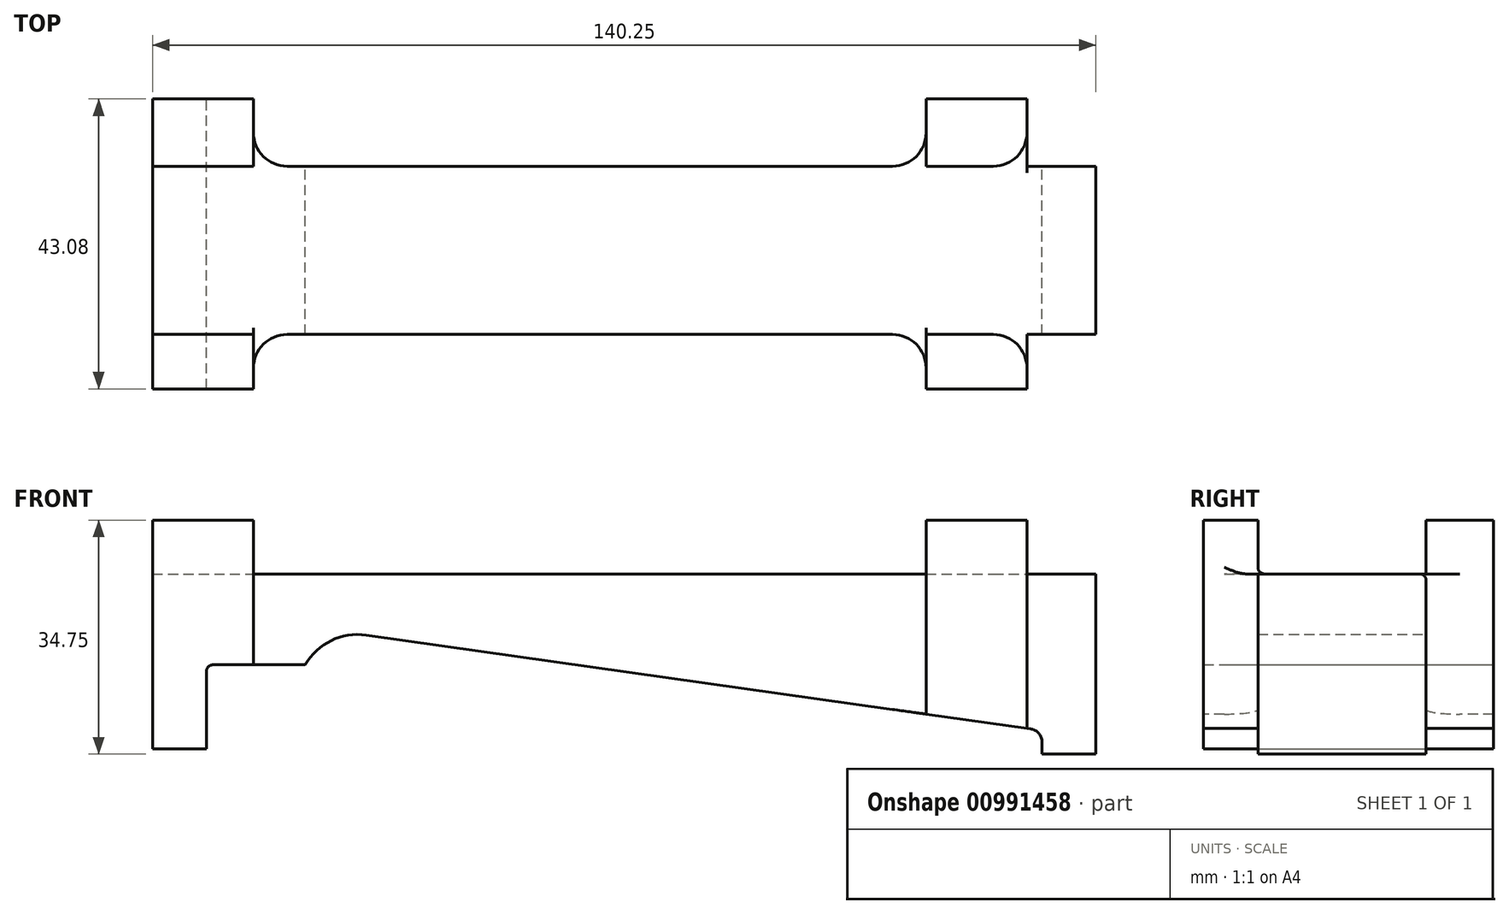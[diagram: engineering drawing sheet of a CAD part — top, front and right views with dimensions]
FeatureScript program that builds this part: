
annotation { "Feature Type Name" : "Feature", "Feature Type Description" : "" }
export const myFeature = defineFeature(function(context is Context, id is Id, definition is map)
    precondition{}
    {
        {
            var Q0;
            Q0=qCreatedBy(makeId("Front.planeOp"),FACE);
            var sketch = newSketch(context, id + "F0", { "sketchPlane" : qUnion([Q0])});
            skLineSegment(sketch, "E0", {"start": v(-65.44, 0) * mm, "end": v(89.84, 0) * mm, "construction": true});
            skArc(sketch, "E1", {"start": v(-48.74, 17.91) * mm, "mid": v(-53.94, 17.1) * mm, "end": v(-57.8, 13.5) * mm});
            skArc(sketch, "E2", {"start": v(51.75, 2) * mm, "mid": v(51.26, 3.31) * mm, "end": v(50.03, 3.98) * mm});
            skLineSegment(sketch, "E3", {"start": v(-48.74, 17.91) * mm, "end": v(50.03, 3.98) * mm});
            skLineSegment(sketch, "E4", {"start": v(-50, 9) * mm, "end": v(-61.37, 9) * mm, "construction": true});
            skPoint(sketch, "E5", {"position": v(-59, 9) * mm});
            skLineSegment(sketch, "E6", {"start": v(-59, 9) * mm, "end": v(-59, 24) * mm, "construction": true});
            skLineSegment(sketch, "E7", {"start": v(-72, 24) * mm, "end": v(-72, 0) * mm, "construction": true});
            skLineSegment(sketch, "E8", {"start": v(-72, 24) * mm, "end": v(-59, 24) * mm, "construction": true});
            skLineSegment(sketch, "E9", {"start": v(-81.75, 40) * mm, "end": v(68.2, 40) * mm, "construction": true});
            skLineSegment(sketch, "E10", {"start": v(-72, 13) * mm, "end": v(-59, 13) * mm, "construction": true});
            skLineSegment(sketch, "E11", {"start": v(-80.5, 27) * mm, "end": v(59.75, 27) * mm});
            skLineSegment(sketch, "E12", {"start": v(59.75, 27) * mm, "end": v(59.75, 0.25) * mm});
            skLineSegment(sketch, "E13", {"start": v(49.75, 2) * mm, "end": v(53.34, 2) * mm, "construction": true});
            skPoint(sketch, "E14", {"position": v(51.75, 2) * mm});
            skLineSegment(sketch, "E15", {"start": v(51.75, 2) * mm, "end": v(51.75, 0.25) * mm});
            skLineSegment(sketch, "E16", {"start": v(51.75, 0.25) * mm, "end": v(59.75, 0.25) * mm});
            skLineSegment(sketch, "E17", {"start": v(-57.8, 13.5) * mm, "end": v(-72.5, 13.5) * mm});
            skLineSegment(sketch, "E18", {"start": v(-72.5, 13.5) * mm, "end": v(-72.5, 1) * mm});
            skLineSegment(sketch, "E19", {"start": v(-72.5, 1) * mm, "end": v(-80.5, 1) * mm});
            skLineSegment(sketch, "E20", {"start": v(-80.5, 1) * mm, "end": v(-80.5, 27) * mm});
            skSolve(sketch);
        }
        {
            var Q0;
            Q0 = qSketchRegion(id + "F0", true);
            extrude(context, id + "F1", {"entities" : qUnion([Q0]), "depth" : 25 * mm, "offsetDistance" : 25 * mm});
        }
        {
            var Q0;
            Q0=makeQuery(id+"F1.opExtrude","SWEPT_FACE",FACE,{"disambiguationData":[OSD([sQuery(id+"F0.wireOp",EDGE,"E20")])]});
            var sketch = newSketch(context, id + "F2", { "sketchPlane" : qUnion([Q0])});
            skLineSegment(sketch, "E21", {"start": v(0, 27) * mm, "end": v(0, 35) * mm});
            skLineSegment(sketch, "E22", {"start": v(0, 35) * mm, "end": v(-10, 35) * mm});
            skLineSegment(sketch, "E23", {"start": v(-10, 35) * mm, "end": v(-10, 1) * mm});
            skLineSegment(sketch, "E24", {"start": v(-10, 1) * mm, "end": v(0, 1) * mm});
            skSolve(sketch);
        }
        {
            var Q0;
            Q0=makeQuery(id+"F2.imprint","IMPRINT",FACE,{"disambiguationData":[TD([[makeQuery(id+"F2.imprint","IMPRINT",EDGE,{"derivedFrom":sQuery(id+"F2.wireOp",EDGE,"E21")}),1.0]])]});
            extrude(context, id + "F3", {"entities" : qUnion([Q0]), "operationType" : NewBodyOperationType.ADD, "oppositeDirection" : true, "depth" : 130 * mm, "offsetDistance" : 25 * mm});
        }
        {
            var Q0;
            {var subQ2=sQuery(id+"F0.wireOp",EDGE,"E20");var subQ5=sQuery(id+"F0.wireOp",EDGE,"E1");var subQ7=sQuery(id+"F2.wireOp",EDGE,"E21");Q0=makeQuery(id+"F3.boolean.opBoolean","SPLIT",FACE,{"disambiguationData":[TD([makeQuery(id+"F1.opExtrude","SWEPT_FACE",FACE,{"disambiguationData":[OSD([subQ5])]})])],"derivedFrom":makeQuery(id+"F3.opExtrude","SWEPT_FACE",FACE,{"disambiguationData":[OSD([subQ2,subQ7])]})});}
            extrude(context, id + "F4", {"entities" : qUnion([Q0]), "operationType" : NewBodyOperationType.REMOVE, "oppositeDirection" : true, "depth" : 25 * mm, "offsetDistance" : 25 * mm});
        }
        {
            var Q0;
            {var subQ0=sQuery(id+"F0.wireOp",EDGE,"E20");var subQ1=sQuery(id+"F2.wireOp",EDGE,"E21");Q0=makeQuery(id+"F3.boolean.opBoolean","SPLIT",EDGE,{"disambiguationData":[topologyDisambiguationEdgeConnected([makeQuery(id+"F1.opExtrude","CAP_FACE",FACE,{"disambiguationData":[OSD([sQuery(id+"F0.wireOp",EDGE,"E1"),sQuery(id+"F0.wireOp",EDGE,"E2"),sQuery(id+"F0.wireOp",EDGE,"E3"),sQuery(id+"F0.wireOp",EDGE,"E11"),sQuery(id+"F0.wireOp",EDGE,"E12"),sQuery(id+"F0.wireOp",EDGE,"E15"),sQuery(id+"F0.wireOp",EDGE,"E16"),sQuery(id+"F0.wireOp",EDGE,"E17"),sQuery(id+"F0.wireOp",EDGE,"E18"),sQuery(id+"F0.wireOp",EDGE,"E19"),subQ0])],"isStart":true}),makeQuery(id+"F3.opExtrude","CAP_FACE",FACE,{"disambiguationData":[OSD([subQ0,subQ1,sQuery(id+"F2.wireOp",EDGE,"E22"),sQuery(id+"F2.wireOp",EDGE,"E23"),sQuery(id+"F2.wireOp",EDGE,"E24")])],"isStart":false})])],"derivedFrom":makeQuery(id+"F3.opExtrude","CAP_EDGE",EDGE,{"disambiguationData":[OSD([subQ0,subQ1])],"isStart":false})});}
            fillet(context, id + "F5", {"entities" : qUnion([Q0]), "radius" : 5 * mm, "tangentPropagation" : true, "allowEdgeOverflow" : false});
        }
        {
            var Q0;
            {var subQ0=sQuery(id+"F0.wireOp",EDGE,"E20");Q0=makeQuery(id+"F3.boolean.opBoolean","MERGE",FACE,{"derivedFrom":[makeQuery(id+"F1.opExtrude","SWEPT_FACE",FACE,{"disambiguationData":[OSD([subQ0])]}),makeQuery(id+"F3.opExtrude","CAP_FACE",FACE,{"disambiguationData":[OSD([subQ0,sQuery(id+"F2.wireOp",EDGE,"E21"),sQuery(id+"F2.wireOp",EDGE,"E22"),sQuery(id+"F2.wireOp",EDGE,"E23"),sQuery(id+"F2.wireOp",EDGE,"E24")])],"isStart":true})]});}
            var sketch = newSketch(context, id + "F6", { "sketchPlane" : qUnion([Q0])});
            skLineSegment(sketch, "E25", {"start": v(25, 27) * mm, "end": v(25, 35) * mm});
            skLineSegment(sketch, "E26", {"start": v(25, 35) * mm, "end": v(33.08, 35) * mm});
            skLineSegment(sketch, "E27", {"start": v(33.08, 35) * mm, "end": v(33.08, 1) * mm});
            skLineSegment(sketch, "E28", {"start": v(25, 1) * mm, "end": v(33.08, 1) * mm});
            skPoint(sketch, "E29.orphan", {"position": v(33.08, 0) * mm});
            skSolve(sketch);
        }
        {
            var Q0;
            Q0 = qSketchRegion(id + "F6", true);
            var Q1;
            Q1=makeQuery(id+"F6.imprint","IMPRINT",FACE,{"disambiguationData":[TD([[makeQuery(id+"F6.imprint","IMPRINT",EDGE,{"derivedFrom":sQuery(id+"F6.wireOp",EDGE,"E25")}),-1.0]])]});
            extrude(context, id + "F7", {"entities" : qUnion([Q0, Q1]), "operationType" : NewBodyOperationType.ADD, "oppositeDirection" : true, "depth" : 130 * mm, "offsetDistance" : 25 * mm});
        }
        {
            var Q0;
            {var subQ2=sQuery(id+"F0.wireOp",EDGE,"E20");var subQ5=sQuery(id+"F0.wireOp",EDGE,"E1");var subQ7=sQuery(id+"F6.wireOp",EDGE,"E25");Q0=makeQuery(id+"F7.boolean.opBoolean","SPLIT",FACE,{"disambiguationData":[TD([makeQuery(id+"F1.opExtrude","SWEPT_FACE",FACE,{"disambiguationData":[OSD([subQ5])]})])],"derivedFrom":makeQuery(id+"F7.opExtrude","SWEPT_FACE",FACE,{"disambiguationData":[OSD([subQ2,subQ7])]})});}
            extrude(context, id + "F8", {"entities" : qUnion([Q0]), "operationType" : NewBodyOperationType.REMOVE, "oppositeDirection" : true, "depth" : 25 * mm, "offsetDistance" : 25 * mm});
        }
        {
            var Q0;
            {var subQ0=sQuery(id+"F0.wireOp",EDGE,"E20");var subQ1=sQuery(id+"F6.wireOp",EDGE,"E25");Q0=makeQuery(id+"F7.boolean.opBoolean","SPLIT",EDGE,{"disambiguationData":[topologyDisambiguationEdgeConnected([makeQuery(id+"F1.opExtrude","CAP_FACE",FACE,{"disambiguationData":[OSD([sQuery(id+"F0.wireOp",EDGE,"E1"),sQuery(id+"F0.wireOp",EDGE,"E2"),sQuery(id+"F0.wireOp",EDGE,"E3"),sQuery(id+"F0.wireOp",EDGE,"E11"),sQuery(id+"F0.wireOp",EDGE,"E12"),sQuery(id+"F0.wireOp",EDGE,"E15"),sQuery(id+"F0.wireOp",EDGE,"E16"),sQuery(id+"F0.wireOp",EDGE,"E17"),sQuery(id+"F0.wireOp",EDGE,"E18"),sQuery(id+"F0.wireOp",EDGE,"E19"),subQ0])],"isStart":false}),makeQuery(id+"F7.opExtrude","CAP_FACE",FACE,{"disambiguationData":[OSD([subQ0,subQ1,sQuery(id+"F6.wireOp",EDGE,"E26"),sQuery(id+"F6.wireOp",EDGE,"E27"),sQuery(id+"F6.wireOp",EDGE,"E28")])],"isStart":false})])],"derivedFrom":makeQuery(id+"F7.opExtrude","CAP_EDGE",EDGE,{"disambiguationData":[OSD([subQ0,subQ1])],"isStart":false})});}
            fillet(context, id + "F9", {"entities" : qUnion([Q0]), "radius" : 5 * mm, "tangentPropagation" : true, "allowEdgeOverflow" : false});
        }
        {
            var Q0;
            {var subQ0=sQuery(id+"F0.wireOp",EDGE,"E18");var subQ1=sQuery(id+"F0.wireOp",EDGE,"E17");Q0=makeQuery(id+"F8.boolean.opBoolean","MERGE",EDGE,{"derivedFrom":[makeQuery(id+"F4.boolean.opBoolean","MERGE",EDGE,{"derivedFrom":[makeQuery(id+"F1.opExtrude","SWEPT_EDGE",EDGE,{"disambiguationData":[OSD([subQ1,subQ0])]})],"fromTools":[makeQuery(id+"F4.opExtrude","SWEPT_EDGE",EDGE,{"disambiguationData":[OSD([subQ1,subQ0])]})]})],"fromTools":[makeQuery(id+"F8.opExtrude","SWEPT_EDGE",EDGE,{"disambiguationData":[OSD([subQ1,subQ0])]})]});}
            fillet(context, id + "F10", {"entities" : qUnion([Q0]), "radius" : 1 * mm, "tangentPropagation" : true, "allowEdgeOverflow" : false});
        }
        {
            var Q0;
            Q0=makeQuery(id+"F3.opExtrude","SWEPT_FACE",FACE,{"disambiguationData":[OSD([sQuery(id+"F2.wireOp",EDGE,"E22")])]});
            var sketch = newSketch(context, id + "F11", { "sketchPlane" : qUnion([Q0])});
            skLineSegment(sketch, "E30", {"start": v(-65.5, 10) * mm, "end": v(-65.5, 0) * mm});
            skLineSegment(sketch, "E31", {"start": v(34.5, 10) * mm, "end": v(34.5, 0) * mm});
            skLineSegment(sketch, "E32", {"start": v(34.5, -24.65) * mm, "end": v(34.5, -33.03) * mm});
            skLineSegment(sketch, "E33", {"start": v(-65.5, -25.14) * mm, "end": v(-65.5, -33.03) * mm});
            skLineSegment(sketch, "E34", {"start": v(-65.5, 10) * mm, "end": v(34.5, 10) * mm});
            skLineSegment(sketch, "E35", {"start": v(-65.5, 0) * mm, "end": v(34.5, 0) * mm});
            skLineSegment(sketch, "E36", {"start": v(-65.5, -25.14) * mm, "end": v(34.5, -24.65) * mm});
            skLineSegment(sketch, "E37", {"start": v(-65.5, -33.03) * mm, "end": v(34.5, -33.03) * mm});
            skSolve(sketch);
        }
        {
            var Q0;
            Q0=makeQuery(id+"F11.imprint","IMPRINT",FACE,{"disambiguationData":[TD([[makeQuery(id+"F11.imprint","IMPRINT",EDGE,{"derivedFrom":sQuery(id+"F11.wireOp",EDGE,"E30")}),1.0]])]});
            extrude(context, id + "F12", {"entities" : qUnion([Q0]), "operationType" : NewBodyOperationType.REMOVE, "oppositeDirection" : true, "depth" : 35 * mm, "offsetDistance" : 25 * mm});
        }
        {
            var Q0;
            Q0=makeQuery(id+"F7.opExtrude","SWEPT_FACE",FACE,{"disambiguationData":[OSD([sQuery(id+"F6.wireOp",EDGE,"E26")])]});
            var sketch = newSketch(context, id + "F13", { "sketchPlane" : qUnion([Q0])});
            skLineSegment(sketch, "E38", {"start": v(-65.5, -25) * mm, "end": v(-65.5, -33.08) * mm});
            skLineSegment(sketch, "E39", {"start": v(34.5, -25) * mm, "end": v(34.5, -33.08) * mm});
            skSolve(sketch);
        }
        {
            var Q0;
            Q0 = qSketchRegion(id + "F13", true);
            var Q1;
            {var subQ0=sQuery(id+"F13.wireOp",EDGE,"E38");Q1=makeQuery(id+"F13.imprint","IMPRINT",FACE,{"disambiguationData":[TD([[makeQuery(id+"F13.imprint","IMPRINT",EDGE,{"derivedFrom":subQ0}),1.0]])]});}
            extrude(context, id + "F14", {"entities" : qUnion([Q0, Q1]), "operationType" : NewBodyOperationType.REMOVE, "oppositeDirection" : true, "depth" : 35 * mm, "offsetDistance" : 25 * mm});
        }
        {
            var Q0;
            {var subQ0=sQuery(id+"F13.wireOp",EDGE,"E39");var subQ1=sQuery(id+"F6.wireOp",EDGE,"E26");var subQ2=sQuery(id+"F6.wireOp",EDGE,"E25");Q0=makeQuery(id+"F14.boolean.opBoolean","COPY",EDGE,{"disambiguationData":[topologyDisambiguationEdgeConnected([makeQuery(id+"F14.opExtrude","SWEPT_FACE",FACE,{"disambiguationData":[OSD([subQ2,subQ1])]})])],"derivedFrom":makeQuery(id+"F14.opExtrude","SWEPT_EDGE",EDGE,{"disambiguationData":[OSD([subQ2,subQ1,subQ0])]})});}
            var Q1;
            {var subQ0=sQuery(id+"F13.wireOp",EDGE,"E38");var subQ1=sQuery(id+"F6.wireOp",EDGE,"E26");var subQ2=sQuery(id+"F6.wireOp",EDGE,"E25");Q1=makeQuery(id+"F14.boolean.opBoolean","COPY",EDGE,{"disambiguationData":[topologyDisambiguationEdgeConnected([makeQuery(id+"F14.opExtrude","SWEPT_FACE",FACE,{"disambiguationData":[OSD([subQ2,subQ1])]})])],"derivedFrom":makeQuery(id+"F14.opExtrude","SWEPT_EDGE",EDGE,{"disambiguationData":[OSD([subQ2,subQ1,subQ0])]})});}
            var Q2;
            {var subQ0=sQuery(id+"F11.wireOp",EDGE,"E30");var subQ1=sQuery(id+"F11.wireOp",EDGE,"E35");Q2=makeQuery(id+"F12.boolean.opBoolean","COPY",EDGE,{"disambiguationData":[topologyDisambiguationEdgeConnected([makeQuery(id+"F12.opExtrude","SWEPT_FACE",FACE,{"disambiguationData":[OSD([subQ1])]})])],"derivedFrom":makeQuery(id+"F12.opExtrude","SWEPT_EDGE",EDGE,{"disambiguationData":[OSD([sQuery(id+"F2.wireOp",EDGE,"E21"),sQuery(id+"F2.wireOp",EDGE,"E22"),subQ0,subQ1])]})});}
            var Q3;
            {var subQ0=sQuery(id+"F11.wireOp",EDGE,"E31");var subQ1=sQuery(id+"F11.wireOp",EDGE,"E35");Q3=makeQuery(id+"F12.boolean.opBoolean","COPY",EDGE,{"disambiguationData":[topologyDisambiguationEdgeConnected([makeQuery(id+"F12.opExtrude","SWEPT_FACE",FACE,{"disambiguationData":[OSD([subQ1])]})])],"derivedFrom":makeQuery(id+"F12.opExtrude","SWEPT_EDGE",EDGE,{"disambiguationData":[OSD([sQuery(id+"F2.wireOp",EDGE,"E21"),sQuery(id+"F2.wireOp",EDGE,"E22"),subQ0,subQ1])]})});}
            fillet(context, id + "F15", {"entities" : qUnion([Q0, Q1, Q2, Q3]), "radius" : 5 * mm, "tangentPropagation" : true, "allowEdgeOverflow" : false});
        }
        {
            var Q0;
            {var subQ0=sQuery(id+"F6.wireOp",EDGE,"E25");var subQ1=sQuery(id+"F0.wireOp",EDGE,"E20");var subQ2=makeQuery(id+"F7.opExtrude","SWEPT_FACE",FACE,{"disambiguationData":[OSD([subQ1,subQ0])]});var subQ4=sQuery(id+"F0.wireOp",EDGE,"E11");var subQ5=makeQuery(id+"F1.opExtrude","SWEPT_FACE",FACE,{"disambiguationData":[OSD([subQ4])]});Q0=makeQuery(id+"F14.boolean.opBoolean","SPLIT",EDGE,{"disambiguationData":[topologyDisambiguationEdgeConnected([subQ5,subQ2]),TD([makeQuery(id+"F14.opExtrude","SWEPT_FACE",FACE,{"disambiguationData":[OSD([sQuery(id+"F13.wireOp",EDGE,"E39")])]})])],"derivedFrom":makeQuery(id+"F7.boolean.opBoolean","SPLIT",EDGE,{"disambiguationData":[topologyDisambiguationEdgeConnected([subQ2])],"derivedFrom":makeQuery(id+"F1.opExtrude","CAP_EDGE",EDGE,{"disambiguationData":[OSD([subQ4])],"isStart":false})})});}
            var Q1;
            {var subQ0=sQuery(id+"F0.wireOp",EDGE,"E20");var subQ2=sQuery(id+"F6.wireOp",EDGE,"E25");var subQ3=sQuery(id+"F0.wireOp",EDGE,"E11");var subQ4=makeQuery(id+"F1.opExtrude","SWEPT_FACE",FACE,{"disambiguationData":[OSD([subQ3])]});var subQ5=makeQuery(id+"F7.opExtrude","SWEPT_FACE",FACE,{"disambiguationData":[OSD([subQ0,subQ2])]});Q1=makeQuery(id+"F14.boolean.opBoolean","SPLIT",EDGE,{"disambiguationData":[topologyDisambiguationEdgeConnected([subQ4,subQ5]),TD([makeQuery(id+"F1.opExtrude","SWEPT_FACE",FACE,{"disambiguationData":[OSD([subQ0])]})])],"derivedFrom":makeQuery(id+"F7.boolean.opBoolean","SPLIT",EDGE,{"disambiguationData":[topologyDisambiguationEdgeConnected([subQ5])],"derivedFrom":makeQuery(id+"F1.opExtrude","CAP_EDGE",EDGE,{"disambiguationData":[OSD([subQ3])],"isStart":false})})});}
            var Q2;
            {var subQ0=sQuery(id+"F2.wireOp",EDGE,"E21");var subQ1=sQuery(id+"F0.wireOp",EDGE,"E20");var subQ2=makeQuery(id+"F3.opExtrude","SWEPT_FACE",FACE,{"disambiguationData":[OSD([subQ1,subQ0])]});var subQ3=sQuery(id+"F0.wireOp",EDGE,"E11");var subQ4=makeQuery(id+"F1.opExtrude","SWEPT_FACE",FACE,{"disambiguationData":[OSD([subQ3])]});Q2=makeQuery(id+"F12.boolean.opBoolean","SPLIT",EDGE,{"disambiguationData":[topologyDisambiguationEdgeConnected([subQ4,subQ2]),TD([makeQuery(id+"F12.opExtrude","SWEPT_FACE",FACE,{"disambiguationData":[OSD([sQuery(id+"F11.wireOp",EDGE,"E31")])]})])],"derivedFrom":makeQuery(id+"F3.boolean.opBoolean","SPLIT",EDGE,{"disambiguationData":[topologyDisambiguationEdgeConnected([subQ2])],"derivedFrom":makeQuery(id+"F1.opExtrude","CAP_EDGE",EDGE,{"disambiguationData":[OSD([subQ3])],"isStart":true})})});}
            var Q3;
            {var subQ0=sQuery(id+"F2.wireOp",EDGE,"E21");var subQ1=sQuery(id+"F0.wireOp",EDGE,"E20");var subQ2=makeQuery(id+"F3.opExtrude","SWEPT_FACE",FACE,{"disambiguationData":[OSD([subQ1,subQ0])]});var subQ3=sQuery(id+"F0.wireOp",EDGE,"E11");var subQ4=makeQuery(id+"F1.opExtrude","SWEPT_FACE",FACE,{"disambiguationData":[OSD([subQ3])]});Q3=makeQuery(id+"F12.boolean.opBoolean","SPLIT",EDGE,{"disambiguationData":[topologyDisambiguationEdgeConnected([subQ4,subQ2]),TD([makeQuery(id+"F1.opExtrude","SWEPT_FACE",FACE,{"disambiguationData":[OSD([subQ1])]})])],"derivedFrom":makeQuery(id+"F3.boolean.opBoolean","SPLIT",EDGE,{"disambiguationData":[topologyDisambiguationEdgeConnected([subQ2])],"derivedFrom":makeQuery(id+"F1.opExtrude","CAP_EDGE",EDGE,{"disambiguationData":[OSD([subQ3])],"isStart":true})})});}
            fillet(context, id + "F16", {"entities" : qUnion([Q0, Q1, Q2, Q3]), "radius" : 1 * mm, "tangentPropagation" : true, "allowEdgeOverflow" : false});
        }
    });
